# Revit family: Шкаф медицинский четырёхдверный полузакрытый ДМ-2-001-13
name_source: partatom
category: Оборудование
revit_build: Autodesk Revit 2017 (Build: 20170118_1100(x64)
units: mm (PartAtom-declared; Revit-internal decimal feet)

## family parameters
Всегда вертикально = Да
На основе рабочей плоскости = Нет
Общий = Нет
При загрузке вырезать с полостями = Нет
Размер круглого соединителя = Использовать диаметр
Тип детали = Нормальный
Точка расчета площади = Нет

## types (2) — shared parameters
Длина ручек = 150 мм
Каркас = Алюминий 7075
Ножки = Пластмасса, непрозрачная, черная
Общ_Высота = 1700 мм
Общ_Глубина = 400 мм
Общ_Единицы измерения = шт.
Общ_Поставщик = Доктор Мебель
Общ_Ширина = 900 мм
Панели = Пластмасса, непрозрачная, белая
Ручки = Алюминий 7075
Стекло = Стекло
Фасад = Столешница медицинской мебели ДСП с пластиковым покрытием

## per-type parameters (varying)
| type | Общ_Наименование | Общ_Тип, марка |
| ЛДСП | Шкаф медицинский четырёхдверный полузакрытый из ЛДСП | ДМ-2-001-13 |
| Полипропилен | Шкаф медицинский четырёхдверный полузакрытый из полипропилена | ДМ-1-001-13 |
